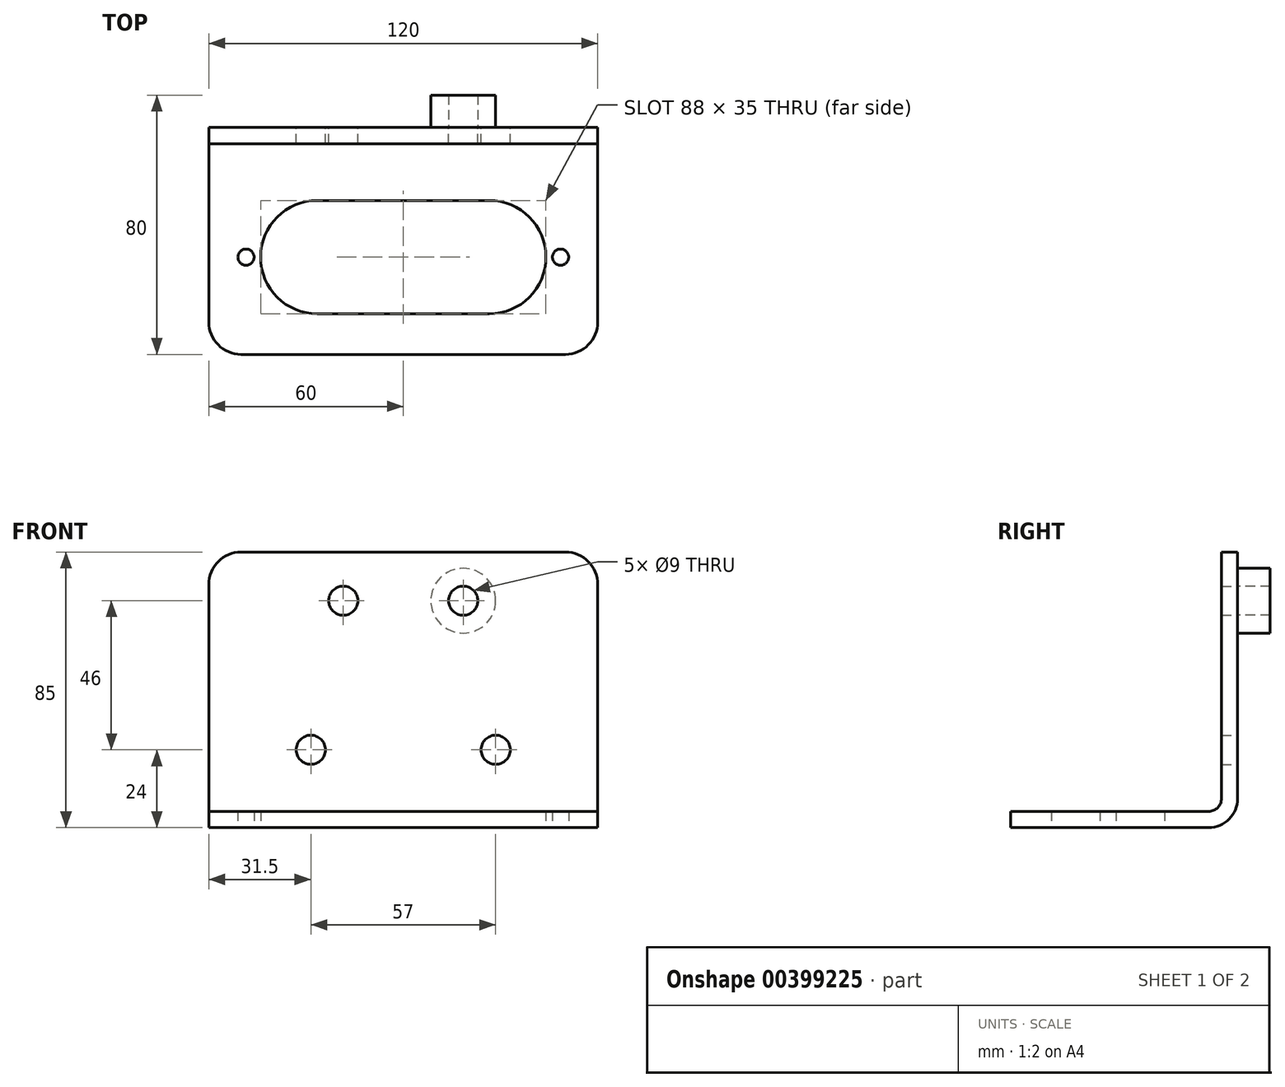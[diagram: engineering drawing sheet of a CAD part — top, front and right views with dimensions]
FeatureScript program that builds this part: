
annotation { "Feature Type Name" : "Feature", "Feature Type Description" : "" }
export const myFeature = defineFeature(function(context is Context, id is Id, definition is map)
    precondition{}
    {
        {
            var Q0;
            Q0=qCreatedBy(makeId("Top.planeOp"),FACE);
            var sketch = newSketch(context, id + "F0", { "sketchPlane" : qUnion([Q0])});
            skLineSegment(sketch, "E0", {"start": v(-60, 0) * mm, "end": v(-60, -60) * mm});
            skArc(sketch, "E1", {"start": v(-60, -60) * mm, "mid": v(-57.07, -67.07) * mm, "end": v(-50, -70) * mm});
            skLineSegment(sketch, "E2", {"start": v(-50, -70) * mm, "end": v(50, -70) * mm});
            skArc(sketch, "E3", {"start": v(50, -70) * mm, "mid": v(57.07, -67.07) * mm, "end": v(60, -60) * mm});
            skLineSegment(sketch, "E4", {"start": v(60, -60) * mm, "end": v(60, 0) * mm});
            skLineSegment(sketch, "E5", {"start": v(60, 0) * mm, "end": v(60, 75) * mm});
            skArc(sketch, "E6", {"start": v(60, 75) * mm, "mid": v(57.07, 82.07) * mm, "end": v(50, 85) * mm});
            skLineSegment(sketch, "E7", {"start": v(50, 85) * mm, "end": v(-50, 85) * mm});
            skArc(sketch, "E8", {"start": v(-50, 85) * mm, "mid": v(-57.07, 82.07) * mm, "end": v(-60, 75) * mm});
            skLineSegment(sketch, "E9", {"start": v(-60, 75) * mm, "end": v(-60, 0) * mm});
            skLineSegment(sketch, "E10", {"start": v(26.5, -22.5) * mm, "end": v(-26.5, -22.5) * mm});
            skArc(sketch, "E11", {"start": v(-26.5, -22.5) * mm, "mid": v(-44, -40) * mm, "end": v(-26.5, -57.5) * mm});
            skLineSegment(sketch, "E12", {"start": v(-26.5, -57.5) * mm, "end": v(26.5, -57.5) * mm});
            skArc(sketch, "E13", {"start": v(26.5, -57.5) * mm, "mid": v(44, -40) * mm, "end": v(26.5, -22.5) * mm});
            skCircle(sketch, "E14", {"center": v(-48.5, -40) * mm, "radius": 2.5 * mm});
            skCircle(sketch, "E15", {"center": v(48.5, -40) * mm, "radius": 2.5 * mm});
            skCircle(sketch, "E16", {"center": v(18.5, 70) * mm, "radius": 4.5 * mm});
            skCircle(sketch, "E17", {"center": v(28.5, 24) * mm, "radius": 4.5 * mm});
            skLineSegment(sketch, "E18", {"start": v(-60, 0) * mm, "end": v(60, 0) * mm});
            skLineSegment(sketch, "E19", {"start": v(-48.5, -40) * mm, "end": v(48.5, -40) * mm, "construction": true});
            skLineSegment(sketch, "E20", {"start": v(0, 85) * mm, "end": v(0, -70) * mm, "construction": true});
            skCircle(sketch, "E21.MirrorC", {"center": v(-18.5, 70) * mm, "radius": 4.5 * mm});
            skCircle(sketch, "E22.MirrorC", {"center": v(-28.5, 24) * mm, "radius": 4.5 * mm});
            skSolve(sketch);
        }
        {
            var Q0;
            Q0=makeQuery(id+"F0.imprint","IMPRINT",FACE,{"disambiguationData":[TD([[makeQuery(id+"F0.imprint","IMPRINT",EDGE,{"derivedFrom":sQuery(id+"F0.wireOp",EDGE,"E0")}),1.0]])]});
            extrude(context, id + "F1", {"entities" : qUnion([Q0]), "depth" : 5 * mm});
        }
        {
            var Q0;
            Q0=makeQuery(id+"F0.imprint","IMPRINT",FACE,{"disambiguationData":[TD([[makeQuery(id+"F0.imprint","IMPRINT",EDGE,{"derivedFrom":sQuery(id+"F0.wireOp",EDGE,"E5")}),1.0]])]});
            extrude(context, id + "F2", {"entities" : qUnion([Q0]), "depth" : 5 * mm});
        }
        {
            var Q0;
            Q0=makeQuery(id+"F2.opExtrude","SWEPT_BODY",BODY,{"disambiguationData":[OSD([sQuery(id+"F0.wireOp",EDGE,"dcd2564a-1519-4e3c-a726-8554a83bfc4d"),sQuery(id+"F0.wireOp",EDGE,"E5"),sQuery(id+"F0.wireOp",EDGE,"E6"),sQuery(id+"F0.wireOp",EDGE,"E7"),sQuery(id+"F0.wireOp",EDGE,"E8"),sQuery(id+"F0.wireOp",EDGE,"E9"),sQuery(id+"F0.wireOp",EDGE,"f265843f-5eec-4993-bfec-df9498e86563"),sQuery(id+"F0.wireOp",EDGE,"E16"),sQuery(id+"F0.wireOp",EDGE,"E17"),sQuery(id+"F0.wireOp",EDGE,"E18")])]});
            var Q1;
            Q1=makeQuery(id+"F1.opExtrude","CAP_EDGE",EDGE,{"disambiguationData":[OSD([sQuery(id+"F0.wireOp",EDGE,"E18")])],"isStart":false});
            transform(context, id + "F3", {"entities" : qUnion([Q0]), "transformType" : TransformType.ROTATION, "transformAxis" : qUnion([Q1]), "angle" : 90 * degree, "makeCopy" : false});
        }
        {
            var Q0;
            Q0=makeQuery(id+"F2.opExtrude","SWEPT_BODY",BODY,{"disambiguationData":[OSD([sQuery(id+"F0.wireOp",EDGE,"dcd2564a-1519-4e3c-a726-8554a83bfc4d"),sQuery(id+"F0.wireOp",EDGE,"E5"),sQuery(id+"F0.wireOp",EDGE,"E6"),sQuery(id+"F0.wireOp",EDGE,"E7"),sQuery(id+"F0.wireOp",EDGE,"E8"),sQuery(id+"F0.wireOp",EDGE,"E9"),sQuery(id+"F0.wireOp",EDGE,"f265843f-5eec-4993-bfec-df9498e86563"),sQuery(id+"F0.wireOp",EDGE,"E16"),sQuery(id+"F0.wireOp",EDGE,"E17"),sQuery(id+"F0.wireOp",EDGE,"E18")])]});
            transform(context, id + "F4", {"entities" : qUnion([Q0]), "transformType" : TransformType.TRANSLATION_3D, "dx" : 0 * mm, "dy" : -5 * mm, "dz" : -5 * mm, "makeCopy" : false});
        }
        {
            var Q0;
            Q0=makeQuery(id+"F1.opExtrude","SWEPT_BODY",BODY,{"disambiguationData":[OSD([sQuery(id+"F0.wireOp",EDGE,"E0"),sQuery(id+"F0.wireOp",EDGE,"E1"),sQuery(id+"F0.wireOp",EDGE,"E2"),sQuery(id+"F0.wireOp",EDGE,"E3"),sQuery(id+"F0.wireOp",EDGE,"E4"),sQuery(id+"F0.wireOp",EDGE,"b944222a-91ae-40db-8da9-c3a74cff1a19"),sQuery(id+"F0.wireOp",EDGE,"52282161-0c92-4602-815b-eede0631a33d"),sQuery(id+"F0.wireOp",EDGE,"E10"),sQuery(id+"F0.wireOp",EDGE,"E11"),sQuery(id+"F0.wireOp",EDGE,"E12"),sQuery(id+"F0.wireOp",EDGE,"E13"),sQuery(id+"F0.wireOp",EDGE,"E14"),sQuery(id+"F0.wireOp",EDGE,"E15"),sQuery(id+"F0.wireOp",EDGE,"E18")])]});
            var Q1;
            Q1=makeQuery(id+"F2.opExtrude","SWEPT_BODY",BODY,{"disambiguationData":[OSD([sQuery(id+"F0.wireOp",EDGE,"dcd2564a-1519-4e3c-a726-8554a83bfc4d"),sQuery(id+"F0.wireOp",EDGE,"E5"),sQuery(id+"F0.wireOp",EDGE,"E6"),sQuery(id+"F0.wireOp",EDGE,"E7"),sQuery(id+"F0.wireOp",EDGE,"E8"),sQuery(id+"F0.wireOp",EDGE,"E9"),sQuery(id+"F0.wireOp",EDGE,"f265843f-5eec-4993-bfec-df9498e86563"),sQuery(id+"F0.wireOp",EDGE,"E16"),sQuery(id+"F0.wireOp",EDGE,"E17"),sQuery(id+"F0.wireOp",EDGE,"E18")])]});
            booleanBodies(context, id + "F5", {"operationType" : BooleanOperationType.UNION, "tools" : qUnion([Q0, Q1])});
        }
        {
            var Q0;
            {var subQ0=sQuery(id+"F0.wireOp",EDGE,"E18");Q0=makeQuery(id+"F5.opBoolean","INTERSECT",EDGE,{"derivedFrom":[makeQuery(id+"F1.opExtrude","CAP_FACE",FACE,{"disambiguationData":[OSD([sQuery(id+"F0.wireOp",EDGE,"E0"),sQuery(id+"F0.wireOp",EDGE,"E1"),sQuery(id+"F0.wireOp",EDGE,"E2"),sQuery(id+"F0.wireOp",EDGE,"E3"),sQuery(id+"F0.wireOp",EDGE,"E4"),sQuery(id+"F0.wireOp",EDGE,"b944222a-91ae-40db-8da9-c3a74cff1a19"),sQuery(id+"F0.wireOp",EDGE,"52282161-0c92-4602-815b-eede0631a33d"),sQuery(id+"F0.wireOp",EDGE,"E10"),sQuery(id+"F0.wireOp",EDGE,"E11"),sQuery(id+"F0.wireOp",EDGE,"E12"),sQuery(id+"F0.wireOp",EDGE,"E13"),sQuery(id+"F0.wireOp",EDGE,"E14"),sQuery(id+"F0.wireOp",EDGE,"E15"),subQ0])],"isStart":false}),makeQuery(id+"F2.opExtrude","CAP_FACE",FACE,{"disambiguationData":[OSD([sQuery(id+"F0.wireOp",EDGE,"dcd2564a-1519-4e3c-a726-8554a83bfc4d"),sQuery(id+"F0.wireOp",EDGE,"E5"),sQuery(id+"F0.wireOp",EDGE,"E6"),sQuery(id+"F0.wireOp",EDGE,"E7"),sQuery(id+"F0.wireOp",EDGE,"E8"),sQuery(id+"F0.wireOp",EDGE,"E9"),sQuery(id+"F0.wireOp",EDGE,"f265843f-5eec-4993-bfec-df9498e86563"),sQuery(id+"F0.wireOp",EDGE,"E16"),sQuery(id+"F0.wireOp",EDGE,"E17"),subQ0])],"isStart":false})]});}
            fillet(context, id + "F6", {"entities" : qUnion([Q0]), "radius" : 4 * mm, "tangentPropagation" : true, "allowEdgeOverflow" : false});
        }
        {
            var Q0;
            Q0=makeQuery(id+"F1.opExtrude","CAP_EDGE",EDGE,{"disambiguationData":[OSD([sQuery(id+"F0.wireOp",EDGE,"E18")])],"isStart":true});
            fillet(context, id + "F7", {"entities" : qUnion([Q0]), "radius" : 9 * mm, "tangentPropagation" : true, "allowEdgeOverflow" : false});
        }
        {
            var Q0;
            {var subQ0=sQuery(id+"F0.wireOp",EDGE,"E18");Q0=makeQuery(id+"F5.opBoolean","MERGE",FACE,{"derivedFrom":[makeQuery(id+"F1.opExtrude","SWEPT_FACE",FACE,{"disambiguationData":[OSD([subQ0])]}),makeQuery(id+"F2.opExtrude","CAP_FACE",FACE,{"disambiguationData":[OSD([sQuery(id+"F0.wireOp",EDGE,"E5"),sQuery(id+"F0.wireOp",EDGE,"E6"),sQuery(id+"F0.wireOp",EDGE,"E7"),sQuery(id+"F0.wireOp",EDGE,"E8"),sQuery(id+"F0.wireOp",EDGE,"E9"),sQuery(id+"F0.wireOp",EDGE,"E16"),sQuery(id+"F0.wireOp",EDGE,"E17"),subQ0])],"isStart":true})]});}
            var sketch = newSketch(context, id + "F8", { "sketchPlane" : qUnion([Q0])});
            skCircle(sketch, "E23.0", {"center": v(-18.5, 70) * mm, "radius": 4.5 * mm});
            skCircle(sketch, "E24", {"center": v(-18.5, 70) * mm, "radius": 10 * mm});
            skSolve(sketch);
        }
        {
            var Q0;
            Q0=qSketchRegion(id+"F8",true);
            extrude(context, id + "F9", {"entities" : qUnion([Q0]), "depth" : 10 * mm});
        }
    });
